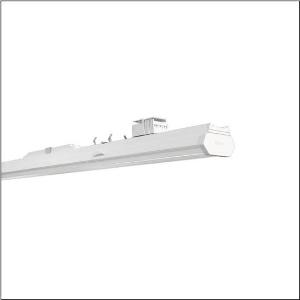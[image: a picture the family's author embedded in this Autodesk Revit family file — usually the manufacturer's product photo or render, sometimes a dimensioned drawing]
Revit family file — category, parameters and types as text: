
# Revit family: licross_r__21_protected_mo_52ts12cn67xf_4b2a
name_source: partatom
category: Lighting Fixtures
units: mm (PartAtom-declared; Revit-internal decimal feet)

## family parameters
Cut with Voids When Loaded = No
Host = Face
Light Source = No
Part Type = Normal
Room Calculation Point = No
Round Connector Dimension = Use Diameter
Shared = No

## types (1)
- --- (1 x LED, 7470 lm, 48.5 W, 6500K)
    Apparent Load = 49 VA
    CIE Flux Codes = 54 82 95 97 100
    Color Rendering = 80
    Color Temperature = 6500K
    Default Elevation = 1800 mm
    Description = Licross® 21 Protected MO, luminaire insert, of sheet steel, galvanised, coil coated, white, length: 1.500mm, width: 90mm, height: 101mm, LED rated luminous flux: 7.460lm, light colour: 865, control gear: ON/OFF Multilumen, CLOi, control gear: ECG Multilumen, with plug, 3-pole, with phase selection, mains connection: 220..240V, AC, 50/60Hz, start of lifetime: 49W, end of service life: 55W, halogen-free wiring, primary optical cover: cover, of PMMA, light emission: direct distribution, primary light characteristic: symmetric, protection rating (complete): IP50, insulation class (complete): insulation class I (protective earthing), certification: CE, ENEC, VDE, UKCA, protection symbol: D if used in an environment with conductive dust loads with corresponding accessories, impact resistance: IK06, permissible ambient temperature for indoor applications: -35..+45°C, corresponds to IFS (International Featured Standards) requirements for safety and quality in the food industry, reducing of maximum allowable ambient temperature of 5°C with ceiling mounting, LABS conformity tested according to VDMA 24364:2018-05, packaging unit: 1 piece
    Height = 92 mm
    Lamp = 1 x LED
    Lamp Light Flux = 7470 lm
    Lamp Power = 48.5 W
    Lamp count = 1
    Length = 1500 mm
    Luminous efficacy = 154 lm/W
    Manufacturer = Siteco
    ModVariant = No
    Model = 52TS12CN67XF
    Mounting Place = Ceiling
    Mounting Type = Pendant
    Number of Poles = 1
    OnlyDefault = Yes
    Power Factor = 1
    Product Name = Licross® 21 Protected MO
    Product group = luminaire insert
    ProductGroupID = 901
    Protection Class = Protection class I
    Protection Degree = IP 50
    RLX_Detail_Level = 1
    RLX_Emergency_Light_Flux = 0 lm
    RLX_Emergency_Type = 0
    RLX_Emergency_Type_DB = No
    RlxData = <blob elided: 21965 chars, md5=d0c4278c>
    Socket = socket
    Standby Power = 0 W
    System Light Flux = 7470 lm
    System Power = 49 W
    Type Comments = factory setting: luminous flux: 100 % | (A | C | E) | 117 mA
    Type Image = l_1256145.jpg
    URL = http://relux.com
    VarID = @adj_131645
    Voltage = 0 V
    Weight = 0.00 kg
    Width = 88 mm

## geometry (parser evidence)
native form markers: Blend x4, Sweep x10
no freeform markers — native parametric forms only
